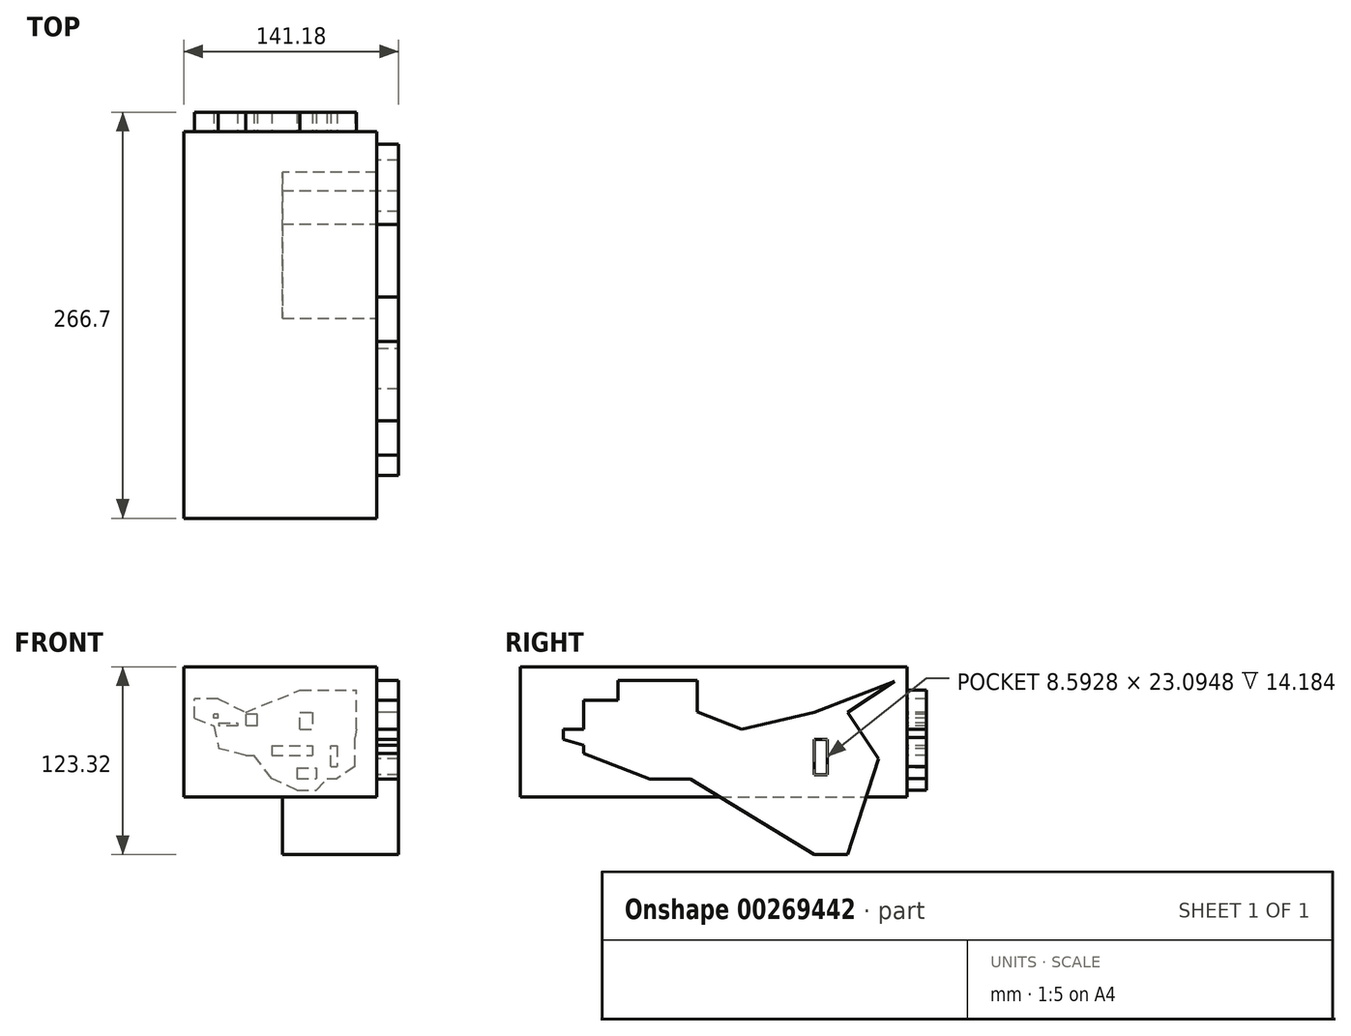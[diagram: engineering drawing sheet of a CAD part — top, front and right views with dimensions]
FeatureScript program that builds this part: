
annotation { "Feature Type Name" : "Feature", "Feature Type Description" : "" }
export const myFeature = defineFeature(function(context is Context, id is Id, definition is map)
    precondition{}
    {
        {
            var Q0;
            Q0=qCreatedBy(makeId("Front.planeOp"),FACE);
            var sketch = newSketch(context, id + "F0", { "sketchPlane" : qUnion([Q0])});
            skLineSegment(sketch, "E0.bottom", {"start": v(-64.98, 40.9) * mm, "end": v(62.02, 40.9) * mm});
            skLineSegment(sketch, "E0.top", {"start": v(-64.98, -44.62) * mm, "end": v(62.02, -44.62) * mm});
            skLineSegment(sketch, "E0.left", {"start": v(-64.98, 40.9) * mm, "end": v(-64.98, -44.62) * mm});
            skLineSegment(sketch, "E0.right", {"start": v(62.02, 40.9) * mm, "end": v(62.02, -44.62) * mm});
            skSolve(sketch);
        }
        {
            var Q0;
            Q0 = qSketchRegion(id + "F0", true);
            extrude(context, id + "F1", {"entities" : qUnion([Q0]), "depth" : 254 * mm});
        }
        {
            var Q0;
            Q0=qCreatedBy(makeId("Right.planeOp"),FACE);
            var sketch = newSketch(context, id + "F2", { "sketchPlane" : qUnion([Q0])});
            skLineSegment(sketch, "E1.bottom", {"start": v(-212.35, 18.92) * mm, "end": v(-157.06, 18.92) * mm});
            skLineSegment(sketch, "E1.top", {"start": v(-212.35, -15.96) * mm, "end": v(-157.06, -15.96) * mm});
            skLineSegment(sketch, "E1.left", {"start": v(-212.35, 18.92) * mm, "end": v(-212.35, -15.96) * mm});
            skLineSegment(sketch, "E1.right", {"start": v(-157.06, 18.92) * mm, "end": v(-157.06, -15.96) * mm});
            skLineSegment(sketch, "E2.bottom", {"start": v(-168.93, 0) * mm, "end": v(-108.45, 0) * mm});
            skLineSegment(sketch, "E2.top", {"start": v(-168.93, -32.65) * mm, "end": v(-108.45, -32.65) * mm});
            skLineSegment(sketch, "E2.left", {"start": v(-168.93, 0) * mm, "end": v(-168.93, -32.65) * mm});
            skLineSegment(sketch, "E2.right", {"start": v(-108.45, 0) * mm, "end": v(-108.45, -32.65) * mm});
            skLineSegment(sketch, "E3.bottom", {"start": v(-116.98, -8.9) * mm, "end": v(-64.29, -8.9) * mm});
            skLineSegment(sketch, "E3.top", {"start": v(-116.98, -21.9) * mm, "end": v(-64.29, -21.9) * mm});
            skLineSegment(sketch, "E3.left", {"start": v(-116.98, -8.9) * mm, "end": v(-116.98, -21.9) * mm});
            skLineSegment(sketch, "E3.right", {"start": v(-64.29, -8.9) * mm, "end": v(-64.29, -21.9) * mm});
            skLineSegment(sketch, "E4", {"start": v(-108.45, 0) * mm, "end": v(-64.29, -8.9) * mm});
            skLineSegment(sketch, "E5", {"start": v(-157.06, 18.92) * mm, "end": v(-108.45, 0) * mm});
            skLineSegment(sketch, "E6", {"start": v(-212.35, -15.96) * mm, "end": v(-168.93, -32.65) * mm});
            skLineSegment(sketch, "E7", {"start": v(-108.45, -32.65) * mm, "end": v(-64.29, -21.9) * mm});
            skSolve(sketch);
        }
        {
            var Q0;
            Q0 = qSketchRegion(id + "F2", true);
            extrude(context, id + "F3", {"entities" : qUnion([Q0]), "operationType" : NewBodyOperationType.ADD, "depth" : 76.2 * mm});
        }
        {
            var Q0;
            Q0=qCreatedBy(makeId("Front.planeOp"),FACE);
            var sketch = newSketch(context, id + "F4", { "sketchPlane" : qUnion([Q0])});
            skLineSegment(sketch, "E8.bottom", {"start": v(-24.2, 11.02) * mm, "end": v(19.64, 11.02) * mm});
            skLineSegment(sketch, "E8.top", {"start": v(-24.2, -17.25) * mm, "end": v(19.64, -17.25) * mm});
            skLineSegment(sketch, "E8.left", {"start": v(-24.2, 11.02) * mm, "end": v(-24.2, -17.25) * mm});
            skLineSegment(sketch, "E8.right", {"start": v(19.64, 11.02) * mm, "end": v(19.64, -17.25) * mm});
            skLineSegment(sketch, "E9.bottom", {"start": v(11.5, 0) * mm, "end": v(48.63, 0) * mm});
            skLineSegment(sketch, "E9.top", {"start": v(11.5, 25.63) * mm, "end": v(48.63, 25.63) * mm});
            skLineSegment(sketch, "E9.left", {"start": v(11.5, 0) * mm, "end": v(11.5, 25.63) * mm});
            skLineSegment(sketch, "E9.right", {"start": v(48.63, 0) * mm, "end": v(48.63, 25.63) * mm});
            skLineSegment(sketch, "E10.bottom", {"start": v(-16.53, 2.16) * mm, "end": v(-45.28, 2.16) * mm});
            skLineSegment(sketch, "E10.top", {"start": v(-16.53, 9.82) * mm, "end": v(-45.28, 9.82) * mm});
            skLineSegment(sketch, "E10.left", {"start": v(-16.53, 2.16) * mm, "end": v(-16.53, 9.82) * mm});
            skLineSegment(sketch, "E10.right", {"start": v(-45.28, 2.16) * mm, "end": v(-45.28, 9.82) * mm});
            skLineSegment(sketch, "E11.bottom", {"start": v(-41.92, 4.07) * mm, "end": v(-29.46, 4.07) * mm});
            skLineSegment(sketch, "E11.top", {"start": v(-41.92, -12.7) * mm, "end": v(-29.46, -12.7) * mm});
            skLineSegment(sketch, "E11.left", {"start": v(-41.92, 4.07) * mm, "end": v(-41.92, -12.7) * mm});
            skLineSegment(sketch, "E11.right", {"start": v(-29.46, 4.07) * mm, "end": v(-29.46, -12.7) * mm});
            skLineSegment(sketch, "E12.bottom", {"start": v(-42.4, 7.19) * mm, "end": v(-57.97, 7.19) * mm});
            skLineSegment(sketch, "E12.top", {"start": v(-42.4, 19.88) * mm, "end": v(-57.97, 19.88) * mm});
            skLineSegment(sketch, "E12.left", {"start": v(-42.4, 7.19) * mm, "end": v(-42.4, 19.88) * mm});
            skLineSegment(sketch, "E12.right", {"start": v(-57.97, 7.19) * mm, "end": v(-57.97, 19.88) * mm});
            skLineSegment(sketch, "E13.bottom", {"start": v(-7.19, -10.78) * mm, "end": v(35.7, -10.78) * mm});
            skLineSegment(sketch, "E13.top", {"start": v(-7.19, -32.34) * mm, "end": v(35.7, -32.34) * mm});
            skLineSegment(sketch, "E13.left", {"start": v(-7.19, -10.78) * mm, "end": v(-7.19, -32.34) * mm});
            skLineSegment(sketch, "E13.right", {"start": v(35.7, -10.78) * mm, "end": v(35.7, -32.34) * mm});
            skLineSegment(sketch, "E14.bottom", {"start": v(9.58, -25.4) * mm, "end": v(22.28, -25.4) * mm});
            skLineSegment(sketch, "E14.top", {"start": v(9.58, -40.24) * mm, "end": v(22.28, -40.24) * mm});
            skLineSegment(sketch, "E14.left", {"start": v(9.58, -25.4) * mm, "end": v(9.58, -40.24) * mm});
            skLineSegment(sketch, "E14.right", {"start": v(22.28, -25.4) * mm, "end": v(22.28, -40.24) * mm});
            skLineSegment(sketch, "E15.bottom", {"start": v(31.62, -24.67) * mm, "end": v(47.67, -24.67) * mm});
            skLineSegment(sketch, "E15.top", {"start": v(31.62, -5.5) * mm, "end": v(47.67, -5.5) * mm});
            skLineSegment(sketch, "E15.left", {"start": v(31.62, -24.67) * mm, "end": v(31.62, -5.5) * mm});
            skLineSegment(sketch, "E15.right", {"start": v(47.67, -24.67) * mm, "end": v(47.67, -5.5) * mm});
            skLineSegment(sketch, "E16", {"start": v(-57.97, 7.19) * mm, "end": v(-45.28, 2.16) * mm});
            skLineSegment(sketch, "E17", {"start": v(-45.28, 2.16) * mm, "end": v(-41.92, -12.7) * mm});
            skLineSegment(sketch, "E18", {"start": v(-57.97, 7.19) * mm, "end": v(-62.38, 29.46) * mm});
            skLineSegment(sketch, "E19", {"start": v(-63.24, 32.58) * mm, "end": v(-57.97, 19.88) * mm});
            skLineSegment(sketch, "E20", {"start": v(-42.4, 19.88) * mm, "end": v(-24.2, 11.02) * mm});
            skLineSegment(sketch, "E21", {"start": v(-24.43, 11.02) * mm, "end": v(11.5, 25.63) * mm});
            skLineSegment(sketch, "E22", {"start": v(11.26, 26.11) * mm, "end": v(40.48, 29.46) * mm});
            skLineSegment(sketch, "E23", {"start": v(40.48, 29.46) * mm, "end": v(48.63, 25.63) * mm});
            skLineSegment(sketch, "E24", {"start": v(48.63, 0) * mm, "end": v(47.67, -5.5) * mm});
            skLineSegment(sketch, "E25", {"start": v(47.67, -24.67) * mm, "end": v(35.7, -32.34) * mm});
            skLineSegment(sketch, "E26", {"start": v(22.28, -40.24) * mm, "end": v(29.23, -32.34) * mm});
            skLineSegment(sketch, "E27", {"start": v(9.58, -40.24) * mm, "end": v(-7.19, -32.34) * mm});
            skLineSegment(sketch, "E28", {"start": v(-7.19, -32.34) * mm, "end": v(-18.68, -17.25) * mm});
            skLineSegment(sketch, "E29", {"start": v(-24.2, -17.25) * mm, "end": v(-29.46, -4.31) * mm});
            skLineSegment(sketch, "E30", {"start": v(-24.2, -17.25) * mm, "end": v(-41.92, -12.7) * mm});
            skSolve(sketch);
        }
        {
            var Q0;
            Q0 = qSketchRegion(id + "F4", true);
            extrude(context, id + "F5", {"entities" : qUnion([Q0]), "operationType" : NewBodyOperationType.ADD, "oppositeDirection" : true, "depth" : 12.7 * mm});
        }
        {
            var Q0;
            Q0=qCreatedBy(makeId("Right.planeOp"),FACE);
            var sketch = newSketch(context, id + "F6", { "sketchPlane" : qUnion([Q0])});
            skLineSegment(sketch, "E31.bottom", {"start": v(-39, 11.04) * mm, "end": v(-61.01, 11.04) * mm});
            skLineSegment(sketch, "E31.top", {"start": v(-39, -82.41) * mm, "end": v(-61.01, -82.41) * mm});
            skLineSegment(sketch, "E31.left", {"start": v(-39, 11.04) * mm, "end": v(-39, -82.41) * mm});
            skLineSegment(sketch, "E31.right", {"start": v(-61.01, 11.04) * mm, "end": v(-61.01, -82.41) * mm});
            skLineSegment(sketch, "E32.bottom", {"start": v(-52.42, -6.68) * mm, "end": v(-146.94, -6.68) * mm});
            skLineSegment(sketch, "E32.top", {"start": v(-52.42, -29.78) * mm, "end": v(-146.94, -29.78) * mm});
            skLineSegment(sketch, "E32.left", {"start": v(-52.42, -6.68) * mm, "end": v(-52.42, -29.78) * mm});
            skLineSegment(sketch, "E32.right", {"start": v(-146.94, -6.68) * mm, "end": v(-146.94, -29.78) * mm});
            skLineSegment(sketch, "E33.bottom", {"start": v(-137.81, -18.5) * mm, "end": v(-189.9, -18.5) * mm});
            skLineSegment(sketch, "E33.top", {"start": v(-137.81, 31.99) * mm, "end": v(-189.9, 31.99) * mm});
            skLineSegment(sketch, "E33.left", {"start": v(-137.81, -18.5) * mm, "end": v(-137.81, 31.99) * mm});
            skLineSegment(sketch, "E33.right", {"start": v(-189.9, -18.5) * mm, "end": v(-189.9, 31.99) * mm});
            skLineSegment(sketch, "E34.bottom", {"start": v(-181.31, 0) * mm, "end": v(-225.89, 0) * mm});
            skLineSegment(sketch, "E34.top", {"start": v(-181.31, -6.68) * mm, "end": v(-225.89, -6.68) * mm});
            skLineSegment(sketch, "E34.left", {"start": v(-181.31, 0) * mm, "end": v(-181.31, -6.68) * mm});
            skLineSegment(sketch, "E34.right", {"start": v(-225.89, 0) * mm, "end": v(-225.89, -6.68) * mm});
            skLineSegment(sketch, "E35", {"start": v(-61.01, 11.04) * mm, "end": v(-137.81, -6.68) * mm});
            skLineSegment(sketch, "E36", {"start": v(-61.01, 11.04) * mm, "end": v(-8.38, 31.45) * mm});
            skLineSegment(sketch, "E37", {"start": v(-8.38, 31.45) * mm, "end": v(-39, 11.04) * mm});
            skLineSegment(sketch, "E38", {"start": v(-39, 11.04) * mm, "end": v(-18.67, -19.45) * mm});
            skLineSegment(sketch, "E39", {"start": v(-18.67, -19.45) * mm, "end": v(-39, -82.41) * mm});
            skLineSegment(sketch, "E40", {"start": v(-61.01, -82.41) * mm, "end": v(-146.94, -29.78) * mm});
            skLineSegment(sketch, "E41", {"start": v(-146.94, -29.78) * mm, "end": v(-225.89, -6.68) * mm});
            skSolve(sketch);
        }
        {
            var Q0;
            Q0 = qSketchRegion(id + "F6", true);
            extrude(context, id + "F7", {"entities" : qUnion([Q0]), "operationType" : NewBodyOperationType.ADD, "depth" : 76.2 * mm});
        }
    });
